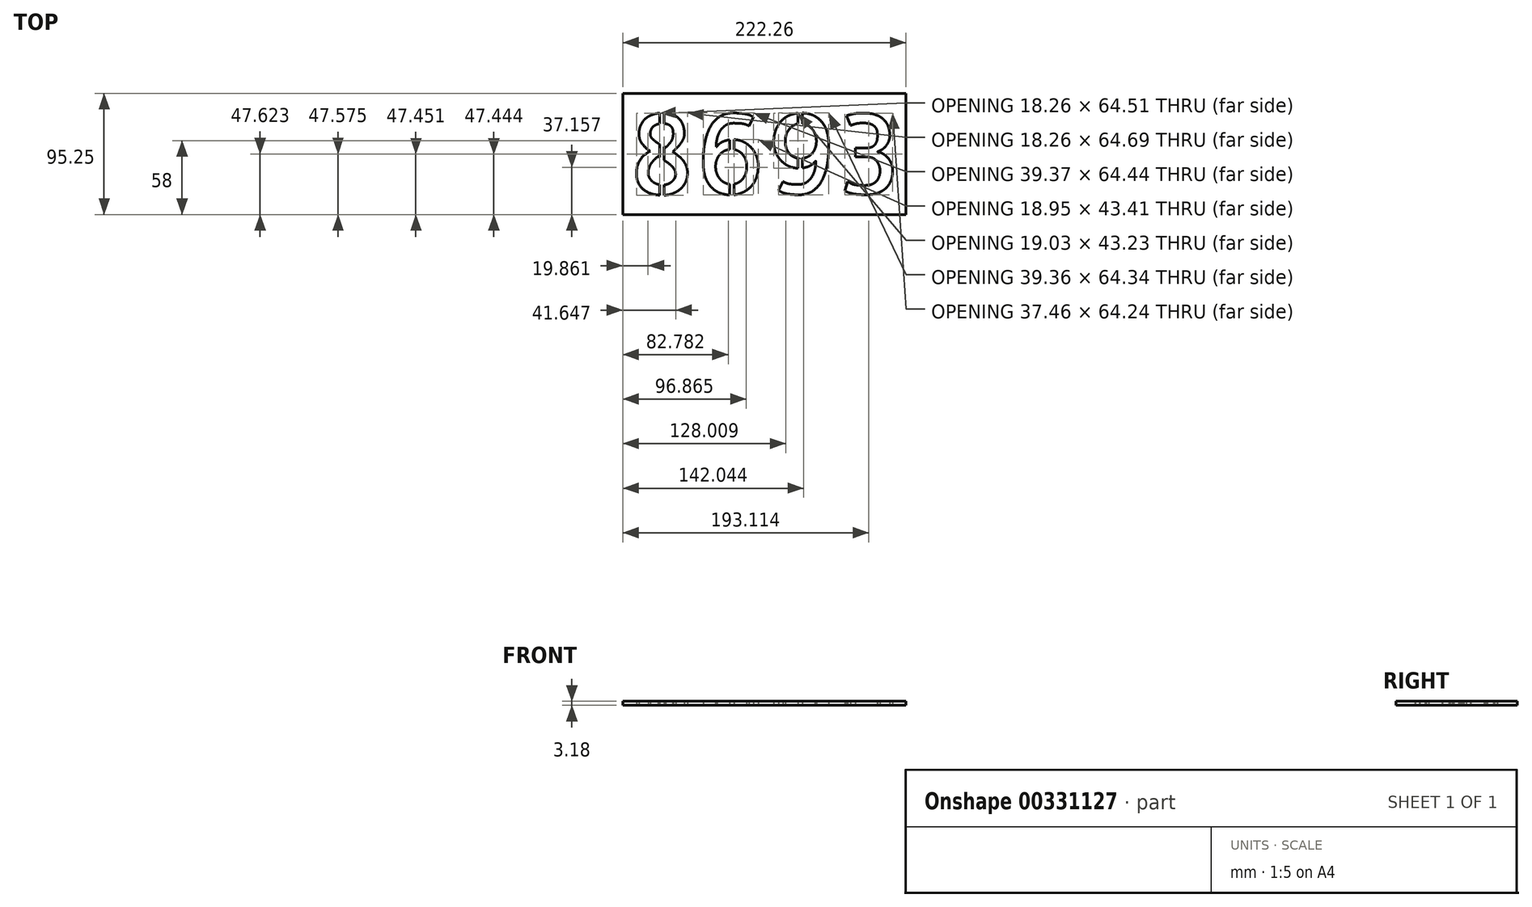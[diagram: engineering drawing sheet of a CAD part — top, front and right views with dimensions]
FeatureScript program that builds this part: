
annotation { "Feature Type Name" : "Feature", "Feature Type Description" : "" }
export const myFeature = defineFeature(function(context is Context, id is Id, definition is map)
    precondition{}
    {
        {
            var Q0;
            Q0=qCreatedBy(makeId("Top.planeOp"),FACE);
            var sketch = newSketch(context, id + "F0", { "sketchPlane" : qUnion([Q0])});
            skLineSegment(sketch, "E0.bottom", {"start": v(-111.13, 43.8) * mm, "end": v(111.13, 43.8) * mm});
            skLineSegment(sketch, "E0.top", {"start": v(-111.13, -51.45) * mm, "end": v(111.13, -51.45) * mm});
            skLineSegment(sketch, "E0.left", {"start": v(-111.13, 43.8) * mm, "end": v(-111.13, -51.45) * mm});
            skLineSegment(sketch, "E0.right", {"start": v(111.13, 43.8) * mm, "end": v(111.13, -51.45) * mm});
            skText(sketch, "E1", { "text": "8693", "fontName": "AllertaStencil-Regular.ttf"});
            const initialGuessF0  = {"E1": [-0.1066, -0.03557, 1, 0, 0.0635]};
            skSetInitialGuess(sketch, initialGuessF0);
            skSolve(sketch);
        }
        {
            var Q0;
            Q0=makeQuery(id+"F0.imprint","IMPRINT",FACE,{"disambiguationData":[TD([[makeQuery(id+"F0.imprint","IMPRINT",EDGE,{"derivedFrom":sQuery(id+"F0.wireOp",EDGE,"E0.bottom")}),-1.0]])]});
            extrude(context, id + "F1", {"entities" : qUnion([Q0]), "depth" : 3.17 * mm, "offsetDistance" : 25.4 * mm});
        }
    });
